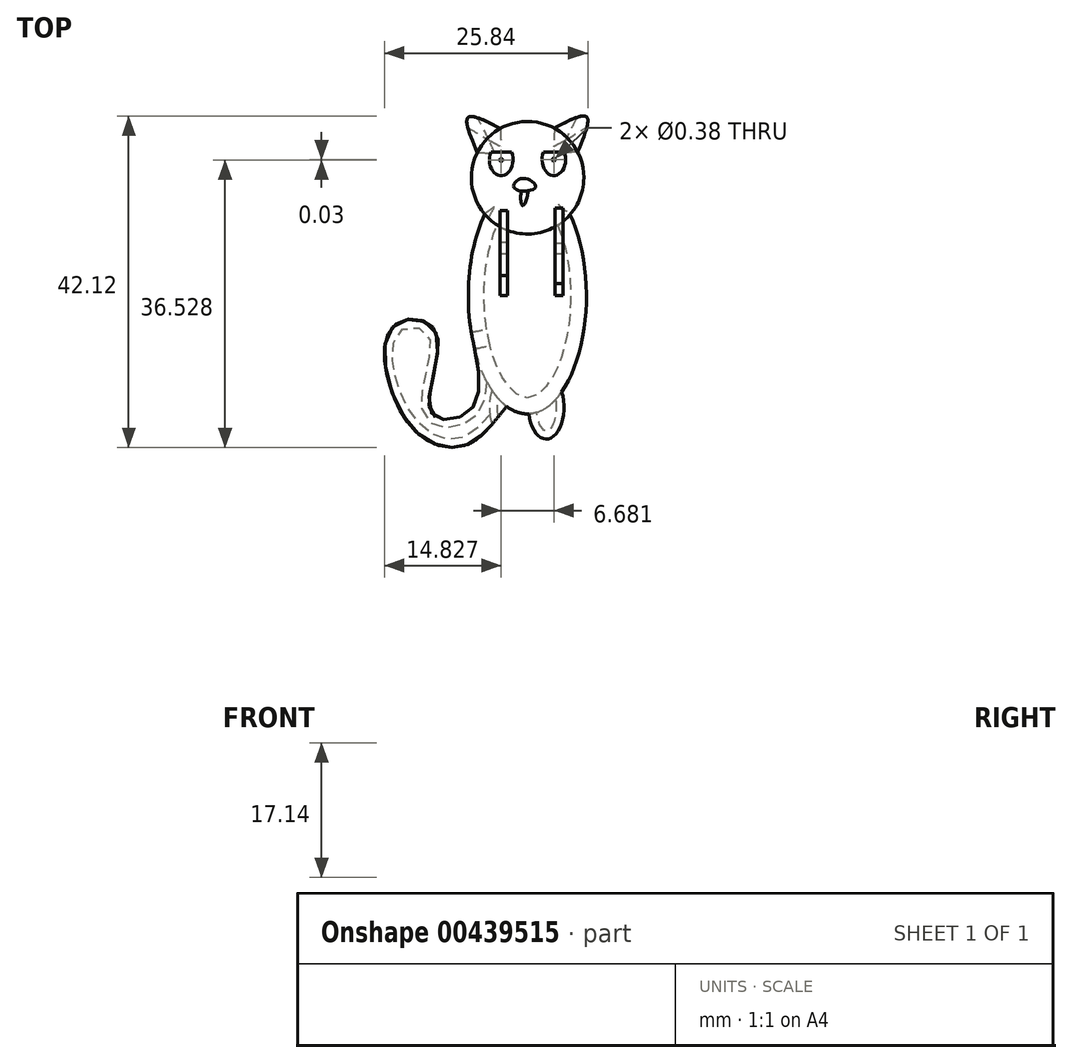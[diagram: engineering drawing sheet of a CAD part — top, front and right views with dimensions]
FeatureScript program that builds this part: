
annotation { "Feature Type Name" : "Feature", "Feature Type Description" : "" }
export const myFeature = defineFeature(function(context is Context, id is Id, definition is map)
    precondition{}
    {
        {
            var Q0;
            Q0=qCreatedBy(makeId("Top.planeOp"),FACE);
            var sketch = newSketch(context, id + "F0", { "sketchPlane" : qUnion([Q0])});
            skEllipticalArc(sketch, "E0", {});
            skFitSpline(sketch, "E1", {"points": [v(-7.14, -4.62) * mm, v(-7.23, -14.53) * mm, v(-12.22, -14.82) * mm, v(-11.64, -4.57) * mm, v(-17.14, -3.98) * mm, v(-14.85, -16.5) * mm, v(-7.76, -18.95) * mm, v(-2.61, -14.06) * mm], "startDerivative": vector(15.83, -77.55) * mm, "endDerivative": vector(37.9, 44.18) * mm});
            skEllipticalArc(sketch, "E2", {});
            skEllipticalArc(sketch, "E3", {});
            skLineSegment(sketch, "E4", {"start": v(0, 21.08) * mm, "end": v(0.2, -21.82) * mm, "construction": true});
            skCircle(sketch, "E5", {"center": v(0.03, 15) * mm, "radius": 7.15 * mm});
            skFitSpline(sketch, "E6", {"points": [v(-6.36, 18.2) * mm, v(-7.54, 22.66) * mm, v(-3.43, 21.26) * mm], "startDerivative": vector(-5.05, 11.73) * mm, "endDerivative": vector(10.99, -5.71) * mm});
            skFitSpline(sketch, "E7.MirrorCS", {"points": [v(6.39, 18.26) * mm, v(7.53, 22.72) * mm, v(3.43, 21.29) * mm], "startDerivative": vector(4.95, 11.77) * mm, "endDerivative": vector(-10.94, -5.81) * mm});
            skEllipticalArc(sketch, "E8", {});
            skEllipticalArc(sketch, "E9.MirrorC", {});
            skLineSegment(sketch, "E10", {"start": v(-4.63, 18.24) * mm, "end": v(-2.02, 18.24) * mm});
            skLineSegment(sketch, "E11.MirrorCS", {"start": v(4.66, 18.28) * mm, "end": v(2.04, 18.26) * mm});
            skFitSpline(sketch, "E12", {"points": [v(-1.65, 13.67) * mm, v(1.03, 13.74) * mm, v(-0.6, 14.91) * mm, v(-1.65, 13.67) * mm]});
            skFitSpline(sketch, "E13", {"points": [v(-0.6, 13.74) * mm, v(-0.6, 11.44) * mm, v(0.03, 13.74) * mm, v(-0.6, 13.74) * mm]});
            skCircle(sketch, "E14", {"center": v(-3.32, 17.26) * mm, "radius": 0.2 * mm});
            skCircle(sketch, "E15.MirrorC", {"center": v(3.36, 17.29) * mm, "radius": 0.2 * mm});
            const initialGuessF0  = {"E0": [0, 0, 0, -1, 0.015, 0.0075, 3.948982155550355, 2.3303799166117187], "E2": [-0.0026147020225384507, -0.014058923619300782, 0, -1, 0.004, 0.002197119072159172, 4.172161652254761, 1.3410497832517345], "E3": [0.0024015977317593255, -0.014210183437916411, 0, -1, 0.004, 0.00225, 4.909851963670488, 2.092649533874315], "E8": [-0.0033234029542654753, 0.017257554456591606, 0, 1, 0.002, 0.0015, 1.0574871419849328, 5.2256981651946495], "E9.MirrorC": [0.0033580468950668656, 0.017287974619566524, -0.009105668107854143, 0.9999585425447947, 0.002, 0.0015, 1.057487141984932, 5.225698165194656]};
            skSetInitialGuess(sketch, initialGuessF0);
            skSolve(sketch);
        }
        {
            var Q0;
            {var subQ1=sQuery(id+"F0.wireOp",EDGE,"E0");var subQ7=sQuery(id+"F0.wireOp",EDGE,"E3");var subQ9=makeQuery(id+"F0.imprint","INTERSECT",VERTEX,{"disambiguationData":[OD(0.0)],"derivedFrom":[subQ1,subQ7]});Q0=makeQuery(id+"F0.imprint","IMPRINT",FACE,{"disambiguationData":[TD([[makeQuery(id+"F0.imprint","IMPRINT",EDGE,{"disambiguationData":[TD([[subQ9,-1.0]])],"derivedFrom":subQ1}),1.0]])]});}
            extrude(context, id + "F1", {"entities" : qUnion([Q0]), "oppositeDirection" : true, "depth" : 4 * mm});
        }
        {
            var Q0;
            Q0=makeQuery(id+"F1.opExtrude","CAP_EDGE",EDGE,{"disambiguationData":[OSD([sQuery(id+"F0.wireOp",EDGE,"E0")])],"isStart":false});
            var Q1;
            Q1=makeQuery(id+"F1.opExtrude","CAP_EDGE",EDGE,{"disambiguationData":[OSD([sQuery(id+"F0.wireOp",EDGE,"E1")])],"isStart":false});
            fillet(context, id + "F2", {"entities" : qUnion([Q0, Q1]), "radius" : 2 * mm, "tangentPropagation" : true, "allowEdgeOverflow" : false});
        }
        {
            var Q0;
            {var subQ0=sQuery(id+"F0.wireOp",EDGE,"E2");var subQ1=sQuery(id+"F0.wireOp",EDGE,"E0");var subQ2=makeQuery(id+"F0.imprint","INTERSECT",VERTEX,{"disambiguationData":[OD(0.0)],"derivedFrom":[subQ1,subQ0]});Q0=makeQuery(id+"F0.imprint","IMPRINT",FACE,{"disambiguationData":[TD([[makeQuery(id+"F0.imprint","IMPRINT",EDGE,{"disambiguationData":[TD([[subQ2,1.0]])],"derivedFrom":subQ1}),-1.0]])]});}
            extrude(context, id + "F3", {"entities" : qUnion([Q0]), "operationType" : NewBodyOperationType.ADD, "oppositeDirection" : true, "depth" : 2 * mm});
        }
        {
            var Q0;
            Q0=makeQuery(id+"F3.opExtrude","CAP_EDGE",EDGE,{"disambiguationData":[OSD([sQuery(id+"F0.wireOp",EDGE,"E1")])],"isStart":false});
            fillet(context, id + "F4", {"entities" : qUnion([Q0]), "radius" : 1 * mm, "tangentPropagation" : true, "allowEdgeOverflow" : false});
        }
        {
            var Q0;
            {var subQ0=sQuery(id+"F0.wireOp",EDGE,"E2");var subQ1=sQuery(id+"F0.wireOp",EDGE,"E0");var subQ2=makeQuery(id+"F0.imprint","INTERSECT",VERTEX,{"disambiguationData":[OD(0.0)],"derivedFrom":[subQ1,subQ0]});Q0=makeQuery(id+"F0.imprint","IMPRINT",FACE,{"disambiguationData":[TD([[makeQuery(id+"F0.imprint","IMPRINT",EDGE,{"disambiguationData":[TD([[subQ2,-1.0]])],"derivedFrom":subQ1}),-1.0]])]});}
            var Q1;
            {var subQ0=sQuery(id+"F0.wireOp",EDGE,"E3");Q1=makeQuery(id+"F0.imprint","IMPRINT",FACE,{"disambiguationData":[TD([[makeQuery(id+"F0.imprint","IMPRINT",EDGE,{"derivedFrom":subQ0}),1.0]])]});}
            extrude(context, id + "F5", {"entities" : qUnion([Q0, Q1]), "operationType" : NewBodyOperationType.ADD, "oppositeDirection" : true, "depth" : 3 * mm});
        }
        {
            var Q0;
            Q0=makeQuery(id+"F5.opExtrude","CAP_EDGE",EDGE,{"disambiguationData":[OSD([sQuery(id+"F0.wireOp",EDGE,"E2")])],"isStart":false});
            var Q1;
            Q1=makeQuery(id+"F5.opExtrude","CAP_EDGE",EDGE,{"disambiguationData":[OSD([sQuery(id+"F0.wireOp",EDGE,"E3")])],"isStart":false});
            fillet(context, id + "F6", {"entities" : qUnion([Q0, Q1]), "radius" : 1 * mm, "tangentPropagation" : true, "allowEdgeOverflow" : false});
        }
        {
            var Q0;
            Q0=qCreatedBy(makeId("Right.planeOp"),FACE);
            cPlane(context, id + "F7", {"entities" : qUnion([Q0]), "cplaneType" : CPlaneType.OFFSET, "offset" : 3.5 * mm, "width" : 150 * mm, "height" : 150 * mm});
        }
        {
            var Q0;
            Q0=qCreatedBy(id+"F7.planeOp",FACE);
            var sketch = newSketch(context, id + "F8", { "sketchPlane" : qUnion([Q0])});
            skFitSpline(sketch, "E16", {"points": [v(5.28, 0) * mm, v(11.1, 6.6) * mm, v(3.33, 13.14) * mm, v(1.7, 11.05) * mm, v(6.54, 6.35) * mm, v(0, 0) * mm], "startDerivative": vector(42.67, 26.54) * mm, "endDerivative": vector(-47.69, -29.45) * mm});
            skLineSegment(sketch, "E17", {"start": v(5.28, 0) * mm, "end": v(0, 0) * mm});
            skSolve(sketch);
        }
        {
            var Q0;
            Q0=makeQuery(id+"F8.imprint","IMPRINT",FACE,{"disambiguationData":[TD([[makeQuery(id+"F8.imprint","IMPRINT",EDGE,{"derivedFrom":sQuery(id+"F8.wireOp",EDGE,"E16")}),1.0]])]});
            extrude(context, id + "F9", {"entities" : qUnion([Q0]), "operationType" : NewBodyOperationType.ADD, "depth" : 1 * mm});
        }
        {
            var Q0;
            Q0=qCreatedBy(makeId("Right.planeOp"),FACE);
            cPlane(context, id + "F10", {"entities" : qUnion([Q0]), "cplaneType" : CPlaneType.OFFSET, "offset" : 3.5 * mm, "oppositeDirection" : true, "width" : 150 * mm, "height" : 150 * mm});
        }
        {
            var Q0;
            Q0=qCreatedBy(id+"F10.planeOp",FACE);
            var sketch = newSketch(context, id + "F11", { "sketchPlane" : qUnion([Q0])});
            skFitSpline(sketch, "E18", {"points": [v(0, 0) * mm, v(6.77, 5.36) * mm, v(2.6, 10.9) * mm, v(4.47, 11.91) * mm, v(10.78, 6.64) * mm, v(5.28, 0) * mm], "startDerivative": vector(46.9, 21.18) * mm, "endDerivative": vector(-38.7, -27.77) * mm});
            skLineSegment(sketch, "E19", {"start": v(5.28, 0) * mm, "end": v(0, 0) * mm});
            skSolve(sketch);
        }
        {
            var Q0;
            Q0=makeQuery(id+"F11.imprint","IMPRINT",FACE,{"disambiguationData":[TD([[makeQuery(id+"F11.imprint","IMPRINT",EDGE,{"derivedFrom":sQuery(id+"F11.wireOp",EDGE,"E18")}),-1.0]])]});
            extrude(context, id + "F12", {"entities" : qUnion([Q0]), "operationType" : NewBodyOperationType.ADD, "depth" : 1 * mm});
        }
        {
            var Q0;
            Q0=makeQuery(id+"F0.imprint","IMPRINT",FACE,{"disambiguationData":[TD([[makeQuery(id+"F0.imprint","IMPRINT",EDGE,{"derivedFrom":sQuery(id+"F0.wireOp",EDGE,"E8")}),-1.0]])]});
            extrude(context, id + "F13", {"entities" : qUnion([Q0]), "operationType" : NewBodyOperationType.ADD, "oppositeDirection" : true, "depth" : 3.5 * mm});
        }
        {
            var Q0;
            Q0=makeQuery(id+"F0.imprint","IMPRINT",FACE,{"disambiguationData":[TD([[makeQuery(id+"F0.imprint","IMPRINT",EDGE,{"derivedFrom":sQuery(id+"F0.wireOp",EDGE,"E8")}),-1.0]])]});
            extrude(context, id + "F14", {"entities" : qUnion([Q0]), "operationType" : NewBodyOperationType.ADD, "depth" : 1 * mm});
        }
        {
            var Q0;
            {var subQ0=sQuery(id+"F0.wireOp",EDGE,"E6");Q0=makeQuery(id+"F0.imprint","IMPRINT",FACE,{"disambiguationData":[TD([[makeQuery(id+"F0.imprint","IMPRINT",EDGE,{"derivedFrom":subQ0}),-1.0]])]});}
            var Q1;
            {var subQ0=sQuery(id+"F0.wireOp",EDGE,"E7.MirrorCS");Q1=makeQuery(id+"F0.imprint","IMPRINT",FACE,{"disambiguationData":[TD([[makeQuery(id+"F0.imprint","IMPRINT",EDGE,{"derivedFrom":subQ0}),1.0]])]});}
            extrude(context, id + "F15", {"entities" : qUnion([Q0, Q1]), "operationType" : NewBodyOperationType.ADD, "oppositeDirection" : true, "depth" : 3.5 * mm});
        }
        {
            var Q0;
            Q0=makeQuery(id+"F0.imprint","IMPRINT",FACE,{"disambiguationData":[TD([[makeQuery(id+"F0.imprint","IMPRINT",EDGE,{"derivedFrom":sQuery(id+"F0.wireOp",EDGE,"E8")}),1.0]])]});
            var Q1;
            Q1=makeQuery(id+"F0.imprint","IMPRINT",FACE,{"disambiguationData":[TD([[makeQuery(id+"F0.imprint","IMPRINT",EDGE,{"derivedFrom":sQuery(id+"F0.wireOp",EDGE,"E9.MirrorC")}),1.0]])]});
            extrude(context, id + "F16", {"entities" : qUnion([Q0, Q1]), "operationType" : NewBodyOperationType.ADD, "oppositeDirection" : true, "depth" : 3.5 * mm});
        }
        {
            var Q0;
            Q0=makeQuery(id+"F0.imprint","IMPRINT",FACE,{"disambiguationData":[TD([[makeQuery(id+"F0.imprint","IMPRINT",EDGE,{"derivedFrom":sQuery(id+"F0.wireOp",EDGE,"E12")}),1.0]])]});
            extrude(context, id + "F17", {"entities" : qUnion([Q0]), "operationType" : NewBodyOperationType.ADD, "oppositeDirection" : true, "depth" : 3.5 * mm});
        }
        {
            var Q0;
            {var subQ0=sQuery(id+"F0.wireOp",EDGE,"E5");var subQ1=makeQuery(id+"F13.opExtrude","SWEPT_FACE",FACE,{"disambiguationData":[OSD([subQ0])]});var subQ2=makeQuery(id+"F13.opExtrude","CAP_FACE",FACE,{"disambiguationData":[OSD([subQ0,sQuery(id+"F0.wireOp",EDGE,"E8"),sQuery(id+"F0.wireOp",EDGE,"E9.MirrorC"),sQuery(id+"F0.wireOp",EDGE,"E10"),sQuery(id+"F0.wireOp",EDGE,"E11.MirrorCS"),sQuery(id+"F0.wireOp",EDGE,"E12")])],"isStart":false});var subQ3=sQuery(id+"F0.wireOp",EDGE,"E3");var subQ4=sQuery(id+"F0.wireOp",EDGE,"E0");var subQ5=makeQuery(id+"F0.imprint","INTERSECT",VERTEX,{"disambiguationData":[OD(0.0)],"derivedFrom":[subQ4,subQ3]});var subQ6=sQuery(id+"F0.wireOp",EDGE,"E2");var subQ8=makeQuery(id+"F0.imprint","INTERSECT",VERTEX,{"disambiguationData":[OD(0.0)],"derivedFrom":[subQ4,subQ6]});var subQ9=makeQuery(id+"F0.imprint","INTERSECT",VERTEX,{"disambiguationData":[OD(1.0)],"derivedFrom":[subQ4,subQ3]});var subQ10=sQuery(id+"F0.wireOp",EDGE,"E7.MirrorCS");Q0=makeQuery(id+"F15.boolean.opBoolean","SPLIT",EDGE,{"disambiguationData":[TD([makeQuery(id+"F1.opExtrude","SWEPT_FACE",FACE,{"disambiguationData":[OSD([subQ0])]}),makeQuery(id+"F2.opFillet","BLEND_FACE",FACE,{"disambiguationData":[OSD([subQ4]),TDD([makeQuery(id+"F1.opExtrude","CAP_EDGE",EDGE,{"disambiguationData":[OSD([subQ4]),TDD([makeQuery(id+"F0.imprint","IMPRINT",EDGE,{"disambiguationData":[TD([[subQ5,-1.0]])],"derivedFrom":subQ4}),makeQuery(id+"F0.imprint","IMPRINT",EDGE,{"disambiguationData":[TD([[subQ9,-1.0]])],"derivedFrom":subQ4}),makeQuery(id+"F0.imprint","IMPRINT",EDGE,{"disambiguationData":[TD([[subQ8,1.0]])],"derivedFrom":subQ4}),makeQuery(id+"F0.imprint","IMPRINT",EDGE,{"disambiguationData":[TD([[subQ8,-1.0]])],"derivedFrom":subQ4}),makeQuery(id+"F0.imprint","IMPRINT",EDGE,{"disambiguationData":[TD([[subQ5,1.0]])],"derivedFrom":subQ4})])],"isStart":false})])]}),subQ1,subQ2,makeQuery(id+"F14.opExtrude","SWEPT_FACE",FACE,{"disambiguationData":[OSD([subQ0])]}),makeQuery(id+"F15.opExtrude","CAP_FACE",FACE,{"disambiguationData":[OSD([subQ0,subQ10])],"isStart":false}),makeQuery(id+"F15.opExtrude","CAP_FACE",FACE,{"disambiguationData":[OSD([subQ0,sQuery(id+"F0.wireOp",EDGE,"E6")])],"isStart":false}),makeQuery(id+"F15.opExtrude","SWEPT_FACE",FACE,{"disambiguationData":[OSD([subQ10])]})])],"derivedFrom":makeQuery(id+"F13.boolean.opBoolean","SPLIT",EDGE,{"disambiguationData":[topologyDisambiguationEdgeConnected([subQ1])],"derivedFrom":makeQuery(id+"F13.opExtrude","CAP_EDGE",EDGE,{"disambiguationData":[OSD([subQ0])],"isStart":false})})});}
            var Q1;
            Q1=makeQuery(id+"F15.opExtrude","CAP_EDGE",EDGE,{"disambiguationData":[OSD([sQuery(id+"F0.wireOp",EDGE,"E7.MirrorCS")])],"isStart":false});
            var Q2;
            {var subQ0=sQuery(id+"F0.wireOp",EDGE,"E7.MirrorCS");var subQ1=sQuery(id+"F0.wireOp",EDGE,"E5");var subQ2=makeQuery(id+"F13.opExtrude","CAP_FACE",FACE,{"disambiguationData":[OSD([subQ1,sQuery(id+"F0.wireOp",EDGE,"E8"),sQuery(id+"F0.wireOp",EDGE,"E9.MirrorC"),sQuery(id+"F0.wireOp",EDGE,"E10"),sQuery(id+"F0.wireOp",EDGE,"E11.MirrorCS"),sQuery(id+"F0.wireOp",EDGE,"E12")])],"isStart":false});var subQ3=makeQuery(id+"F13.opExtrude","SWEPT_FACE",FACE,{"disambiguationData":[OSD([subQ1])]});var subQ4=sQuery(id+"F0.wireOp",EDGE,"E6");Q2=makeQuery(id+"F15.boolean.opBoolean","SPLIT",EDGE,{"disambiguationData":[TD([subQ3,subQ2,makeQuery(id+"F14.opExtrude","SWEPT_FACE",FACE,{"disambiguationData":[OSD([subQ1])]}),makeQuery(id+"F15.opExtrude","CAP_FACE",FACE,{"disambiguationData":[OSD([subQ1,subQ0])],"isStart":false}),makeQuery(id+"F15.opExtrude","CAP_FACE",FACE,{"disambiguationData":[OSD([subQ1,subQ4])],"isStart":false}),makeQuery(id+"F15.opExtrude","SWEPT_FACE",FACE,{"disambiguationData":[OSD([subQ4])]}),makeQuery(id+"F15.opExtrude","SWEPT_FACE",FACE,{"disambiguationData":[OSD([subQ0])]})])],"derivedFrom":makeQuery(id+"F13.boolean.opBoolean","SPLIT",EDGE,{"disambiguationData":[topologyDisambiguationEdgeConnected([subQ3])],"derivedFrom":makeQuery(id+"F13.opExtrude","CAP_EDGE",EDGE,{"disambiguationData":[OSD([subQ1])],"isStart":false})})});}
            var Q3;
            Q3=makeQuery(id+"F15.opExtrude","CAP_EDGE",EDGE,{"disambiguationData":[OSD([sQuery(id+"F0.wireOp",EDGE,"E6")])],"isStart":false});
            var Q4;
            {var subQ0=sQuery(id+"F0.wireOp",EDGE,"E5");var subQ1=makeQuery(id+"F13.opExtrude","CAP_FACE",FACE,{"disambiguationData":[OSD([subQ0,sQuery(id+"F0.wireOp",EDGE,"E8"),sQuery(id+"F0.wireOp",EDGE,"E9.MirrorC"),sQuery(id+"F0.wireOp",EDGE,"E10"),sQuery(id+"F0.wireOp",EDGE,"E11.MirrorCS"),sQuery(id+"F0.wireOp",EDGE,"E12")])],"isStart":false});var subQ2=makeQuery(id+"F13.opExtrude","SWEPT_FACE",FACE,{"disambiguationData":[OSD([subQ0])]});var subQ3=sQuery(id+"F0.wireOp",EDGE,"E6");var subQ4=sQuery(id+"F0.wireOp",EDGE,"E0");Q4=makeQuery(id+"F15.boolean.opBoolean","SPLIT",EDGE,{"disambiguationData":[TD([makeQuery(id+"F1.opExtrude","SWEPT_FACE",FACE,{"disambiguationData":[OSD([subQ0])]}),makeQuery(id+"F2.opFillet","BLEND_FACE",FACE,{"disambiguationData":[OSD([subQ4]),TDD([makeQuery(id+"F1.opExtrude","CAP_EDGE",EDGE,{"disambiguationData":[OSD([subQ4]),TDD([makeQuery(id+"F0.imprint","IMPRINT",EDGE,{"disambiguationData":[TD([[makeQuery(id+"F0.imprint","INTERSECT",VERTEX,{"disambiguationData":[OD(0.0)],"derivedFrom":[subQ4,sQuery(id+"F0.wireOp",EDGE,"E1")]}),1.0]])],"derivedFrom":subQ4})])],"isStart":false})])]}),subQ2,subQ1,makeQuery(id+"F14.opExtrude","SWEPT_FACE",FACE,{"disambiguationData":[OSD([subQ0])]}),makeQuery(id+"F15.opExtrude","CAP_FACE",FACE,{"disambiguationData":[OSD([subQ0,sQuery(id+"F0.wireOp",EDGE,"E7.MirrorCS")])],"isStart":false}),makeQuery(id+"F15.opExtrude","CAP_FACE",FACE,{"disambiguationData":[OSD([subQ0,subQ3])],"isStart":false}),makeQuery(id+"F15.opExtrude","SWEPT_FACE",FACE,{"disambiguationData":[OSD([subQ3])]})])],"derivedFrom":makeQuery(id+"F13.boolean.opBoolean","SPLIT",EDGE,{"disambiguationData":[topologyDisambiguationEdgeConnected([subQ2])],"derivedFrom":makeQuery(id+"F13.opExtrude","CAP_EDGE",EDGE,{"disambiguationData":[OSD([subQ0])],"isStart":false})})});}
            fillet(context, id + "F18", {"entities" : qUnion([Q0, Q1, Q2, Q3, Q4]), "radius" : 2 * mm, "tangentPropagation" : true, "allowEdgeOverflow" : false});
        }
        {
            var Q0;
            Q0=sQuery(id+"F0.wireOp",EDGE,"E14");
            var Q1;
            Q1=sQuery(id+"F0.wireOp",EDGE,"E15.MirrorC");
            extrude(context, id + "F19", {"bodyType" : ToolBodyType.SURFACE, "operationType" : NewBodyOperationType.ADD, "surfaceEntities" : qUnion([Q0, Q1]), "oppositeDirection" : true, "depth" : 3.5 * mm});
        }
        {
            var Q0;
            {var subQ0=sQuery(id+"F0.wireOp",EDGE,"E12");var subQ1=sQuery(id+"F0.wireOp",EDGE,"E11.MirrorCS");var subQ2=sQuery(id+"F0.wireOp",EDGE,"E9.MirrorC");var subQ3=sQuery(id+"F0.wireOp",EDGE,"E10");var subQ4=sQuery(id+"F0.wireOp",EDGE,"E8");var subQ5=sQuery(id+"F0.wireOp",EDGE,"E5");Q0=makeQuery(id+"F17.boolean.opBoolean","MERGE",FACE,{"derivedFrom":[makeQuery(id+"F16.boolean.opBoolean","MERGE",FACE,{"derivedFrom":[makeQuery(id+"F15.boolean.opBoolean","MERGE",FACE,{"derivedFrom":[makeQuery(id+"F13.opExtrude","CAP_FACE",FACE,{"disambiguationData":[OSD([subQ5,subQ4,subQ2,subQ3,subQ1,subQ0])],"isStart":false}),makeQuery(id+"F15.opExtrude","CAP_FACE",FACE,{"disambiguationData":[OSD([subQ5,sQuery(id+"F0.wireOp",EDGE,"E7.MirrorCS")])],"isStart":false}),makeQuery(id+"F15.opExtrude","CAP_FACE",FACE,{"disambiguationData":[OSD([subQ5,sQuery(id+"F0.wireOp",EDGE,"E6")])],"isStart":false})]}),makeQuery(id+"F16.opExtrude","CAP_FACE",FACE,{"disambiguationData":[OSD([subQ4,subQ3,sQuery(id+"F0.wireOp",EDGE,"E14")])],"isStart":false}),makeQuery(id+"F16.opExtrude","CAP_FACE",FACE,{"disambiguationData":[OSD([subQ2,subQ1,sQuery(id+"F0.wireOp",EDGE,"E15.MirrorC")])],"isStart":false})]}),makeQuery(id+"F17.opExtrude","CAP_FACE",FACE,{"disambiguationData":[OSD([subQ0])],"isStart":false})]});}
            extrude(context, id + "F20", {"entities" : qUnion([Q0]), "operationType" : NewBodyOperationType.ADD, "oppositeDirection" : true, "depth" : 0.5 * mm});
        }
    });
